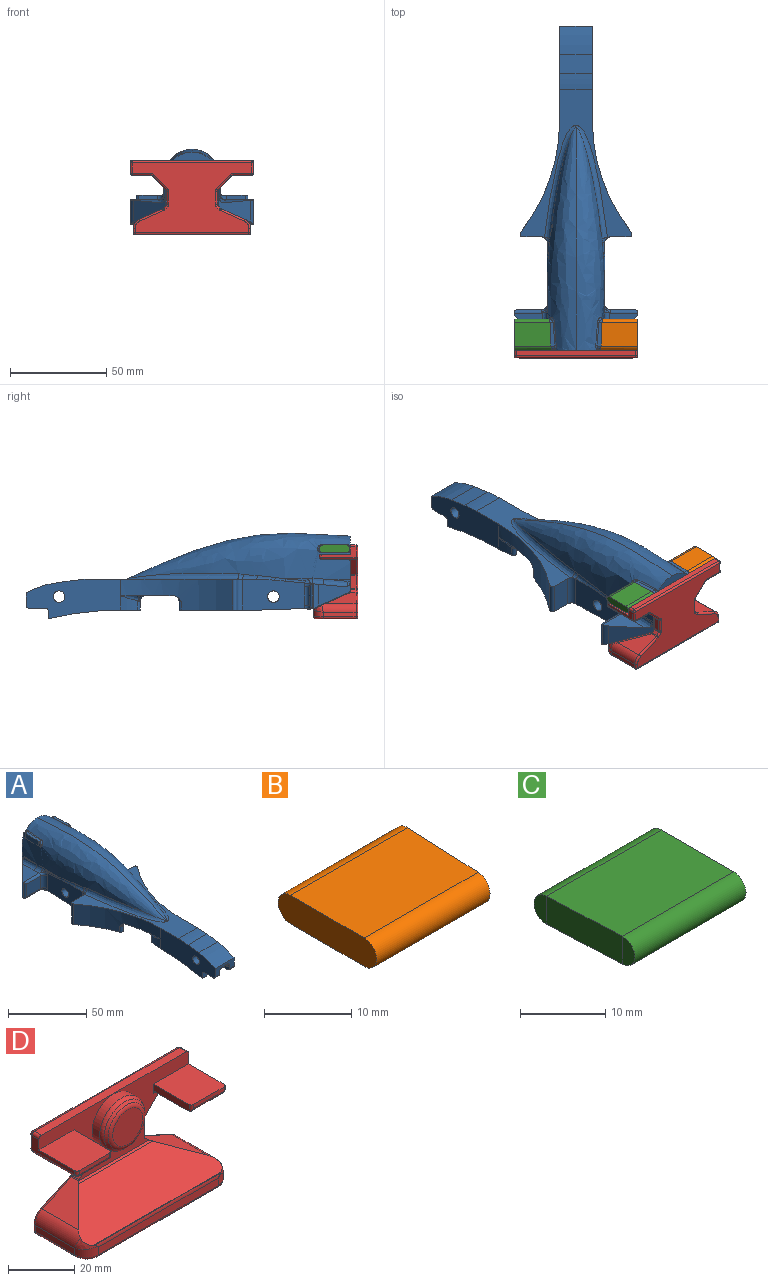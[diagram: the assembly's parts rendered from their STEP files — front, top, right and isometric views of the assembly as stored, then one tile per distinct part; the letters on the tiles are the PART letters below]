
ASSEMBLY  parts=4 mates=3
PART A: 206 faces, bbox 65.7x176.7x49.3 mm
  f0: extruded ~13.86x1.47mm, area 8mm2, adj f153,f156,f180,f181
  f1: extruded ~13.86x1.47mm, area 8mm2, adj f153,f154,f200,f201
  f2: plane 4.04x2.22mm, normal (-1,0.05,0), area 7.2mm2, adj f154,f158,f159,f167,f179
  f3: plane 3.74x2.02mm, normal (-1,0.04,0), area 6.6mm2, adj f4,f154,f158,f166,f174
  f4: plane 1.69x0.12mm, normal (0,-1,0), area 0.1mm2, adj f3,f154,f174
  f5: plane 12x2.55mm, normal (0,0,1), area 21.9mm2, adj f158,f166,f167,f176
  f6: plane 3.74x2.02mm, normal (1,0.04,0), area 6.6mm2, adj f156,f160,f161,f165,f168
  f7: plane 4.04x2.22mm, normal (1,0.05,0), area 7.2mm2, adj f8,f156,f160,f164,f173
  f8: plane 0.69x0.38mm, normal (0,1,0), area 0.1mm2, adj f7,f164,f173
  f9: plane 12x2.55mm, normal (0,0,1), area 21.9mm2, adj f160,f164,f165,f170
  f10: cylinder r=1.5mm len=7.39mm, axis (-1,0,0), area 10mm2, adj f93,f94,f141,f153
  f11: plane 77.19x58.27mm, normal (0,0,1), area 850.3mm2, adj f37,f38,f43,f45,f46,f47,f51,f52
  f12: cylinder r=1.5mm len=7.39mm, axis (-1,0,0), area 10mm2, adj f27,f84,f129,f153
  f13: plane 16.53x15.09mm, normal (0,0.09,1), area 127mm2, adj f94,f95,f96,f97,f144,f181,f182
  f14: cylinder r=3mm len=17mm, axis (-1,0,0), area 320.4mm2, adj f37,f38
  f15: plane 12.39x5.01mm, normal (0,-0.38,-0.93), area 40.5mm2, adj f16,f69,f99,f100,f101,f109,f110,f111
  f16: cylinder r=3mm len=9.64mm, axis (0,0.93,-0.38), area 38.5mm2, adj f15,f35,f39,f99,f150,f151
  f17: plane 32.43x16.02mm, normal (-1,0,0), area 455.3mm2, adj f31,f44,f64,f76,f82,f145,f146,f147
  f18: plane 17.44x4.22mm, normal (-1,0,0), area 15.6mm2, adj f92,f93,f98,f141
  f19: plane 17.44x4.22mm, normal (1,0,0), area 15.6mm2, adj f27,f28,f82,f129
  f20: plane 8.07x3.26mm, normal (-1,0,0), area 12.7mm2, adj f35,f61,f66,f109
  f21: plane 46.27x9mm, normal (1,0,0), area 142.9mm2, adj f41,f59,f67,f77,f78,f101,f102,f103
  f22: plane 38.6x16.7mm, normal (0,0.24,-0.97), area 601mm2, adj f71,f129,f130,f140,f141,f153
  f23: plane 28.21x4.5mm, normal (1,0,0), area 94.2mm2, adj f31,f50,f76,f123,f124,f125
  f24: cylinder r=30mm len=4.5mm, axis (0,0,-1), area 0.2mm2, adj f32,f54,f75,f133
  f25: plane 12.69x9.72mm, normal (0,-1,0), area 123.3mm2, adj f28,f30,f83,f146
  f26: plane 16.53x15.09mm, normal (0,0.09,1), area 127mm2, adj f30,f84,f85,f87,f147,f199,f200
  f27: plane 22.85x18.63mm, normal (0,0.41,-0.91), area 265.4mm2, adj f12,f19,f28,f84,f85,f129
  f28: cylinder r=1.5mm len=21.69mm, axis (-1,0,0), area 45.4mm2, adj f19,f25,f27,f29,f82,f83,f85,f86
  f29: plane 12.72x0.14mm, normal (-1,0,0), area 1.8mm2, adj f28,f30,f83,f86
  f30: cylinder r=1.5mm len=14.19mm, axis (1,0,0), area 34.1mm2, adj f25,f26,f29,f83,f86,f147
  f31: cylinder r=41.69mm len=4.5mm, axis (1,0,0), area 6.5mm2, adj f17,f23,f76,f82,f126
  f32: plane 28.21x4.5mm, normal (-1,0,0), area 94.2mm2, adj f24,f75,f81,f134,f135,f136
  f33: plane 51.59x25.23mm, normal (0,0,-1), area 736.5mm2, adj f45,f51,f73,f74,f105,f106,f116,f117
  f34: plane 46.27x9mm, normal (-1,0,0), area 142.9mm2, adj f40,f56,f65,f79,f80,f112,f113,f114
  f35: plane 17.01x6.48mm, normal (0,-1,0), area 69.2mm2, adj f16,f20,f37,f38,f39,f60,f61,f62
  f36: plane 32.44x16.02mm, normal (1,0,0), area 455.3mm2, adj f44,f63,f75,f81,f98,f142,f143,f144
  f37: plane 49.36x20.5mm, normal (-1,0,0), area 732.8mm2, adj f11,f14,f35,f41,f42,f43,f45,f58
  f38: plane 49.36x20.5mm, normal (1,0,0), area 732.8mm2, adj f11,f14,f35,f40,f42,f43,f51,f57
  f39: plane 8.07x3.26mm, normal (1,0,0), area 12.7mm2, adj f16,f35,f62,f68
  f40: plane 4x4mm, normal (0,-1,0), area 16mm2, adj f34,f38,f65,f79
  f41: plane 4x4mm, normal (0,-1,0), area 16mm2, adj f21,f37,f67,f78
  f42: plane 17x9.65mm, normal (0,-0.14,0.99), area 165.7mm2, adj f37,f38,f43,f60
  f43: cylinder r=60mm len=17mm, axis (1,0,0), area 144.7mm2, adj f11,f37,f38,f42
  f44: cylinder r=3mm len=30mm, axis (-1,0,0), area 565.5mm2, adj f17,f36
  f45: cylinder r=92.82mm len=57.94mm, axis (0,0,1), area 767.9mm2, adj f11,f33,f37,f47,f49,f76,f107,f108
  f46: plane 16x9.64mm, normal (0,1,0), area 154.2mm2, adj f11,f47,f64,f76
  f47: cylinder r=1.5mm len=16mm, axis (0,0,1), area 53.9mm2, adj f11,f45,f46,f76
  f48: cylinder r=136.18mm len=12.06mm, axis (0,0,-1), area 54.3mm2, adj f49,f50,f76,f121
  f49: cylinder r=1.5mm len=4.5mm, axis (0,0,1), area 18.3mm2, adj f45,f48,f76,f120
  f50: cylinder r=30mm len=4.5mm, axis (0,0,-1), area 0.2mm2, adj f23,f48,f76,f122
  f51: cylinder r=92.82mm len=57.94mm, axis (0,0,1), area 767.9mm2, adj f11,f33,f38,f53,f55,f75,f118,f119
  f52: plane 16x9.64mm, normal (0,1,0), area 154.2mm2, adj f11,f53,f63,f75
  f53: cylinder r=1.5mm len=16mm, axis (0,0,1), area 53.9mm2, adj f11,f51,f52,f75
  f54: cylinder r=136.18mm len=12.06mm, axis (0,0,-1), area 54.3mm2, adj f24,f55,f75,f132
  f55: cylinder r=1.5mm len=4.5mm, axis (0,0,1), area 18.3mm2, adj f51,f54,f75,f131
  f56: cylinder r=1.5mm len=4.84mm, axis (0,0,-1), area 19.8mm2, adj f34,f57,f80,f117,f118
  f57: cylinder r=37.75mm len=8.81mm, axis (0,0,-1), area 54.8mm2, adj f38,f56,f80,f119
  f58: cylinder r=37.75mm len=8.81mm, axis (0,0,-1), area 54.8mm2, adj f37,f59,f77,f108
  f59: cylinder r=1.5mm len=4.84mm, axis (0,0,-1), area 19.8mm2, adj f21,f58,f77,f106,f107
  f60: cylinder r=42.58mm len=17mm, axis (-1,0,0), area 268.4mm2, adj f35,f37,f38,f42
  f61: cylinder r=1.5mm len=4mm, axis (-1,0,0), area 9.4mm2, adj f20,f35,f38,f66
  f62: cylinder r=1.5mm len=4mm, axis (-1,0,0), area 9.4mm2, adj f35,f37,f39,f68
  f63: cylinder r=3mm len=16mm, axis (0,0,1), area 75.4mm2, adj f11,f36,f52,f75,f189
  f64: cylinder r=3mm len=16mm, axis (0,0,1), area 75.4mm2, adj f11,f17,f46,f76,f192
  f65: cylinder r=1.5mm len=4mm, axis (-1,0,0), area 9.4mm2, adj f34,f38,f40,f66,f111
  f66: plane 8.57x4.03mm, normal (0,0,-1), area 34.2mm2, adj f20,f38,f61,f65,f110
  f67: cylinder r=1.5mm len=4mm, axis (-1,0,0), area 9.4mm2, adj f21,f37,f41,f68,f100
  f68: plane 8.57x4.03mm, normal (0,0,-1), area 34.2mm2, adj f37,f39,f62,f67,f99
  f69: cylinder r=6mm len=3.81mm, axis (1,0,0), area 11.6mm2, adj f15,f70,f102,f113
  f70: plane 17.07x4.58mm, normal (0,0.26,-0.97), area 53mm2, adj f69,f74,f103,f114
  f71: cylinder r=6mm len=16.69mm, axis (1,0,0), area 55.6mm2, adj f22,f72,f128,f139
  f72: plane 16.03x10.19mm, normal (0,-0.32,-0.95), area 163.1mm2, adj f71,f73,f125,f126,f127,f136,f137,f138
  f73: cylinder r=50mm len=16.18mm, axis (-1,0,0), area 247.2mm2, adj f33,f72,f124,f135
  f74: cylinder r=50mm len=12.97mm, axis (1,0,0), area 39.3mm2, adj f33,f70,f104,f115
  f75: plane 40.66x18.64mm, normal (0,0,-1), area 358mm2, adj f24,f32,f36,f51,f52,f53,f54,f55
  f76: plane 40.66x18.64mm, normal (0,0,-1), area 358mm2, adj f17,f23,f31,f45,f46,f47,f48,f49
  f77: plane 9.96x4mm, normal (0,0,-1), area 34.7mm2, adj f21,f58,f59,f78
  f78: cylinder r=161.13mm len=37.81mm, axis (-1,0,0), area 152.7mm2, adj f21,f37,f41,f77
  f79: cylinder r=161.13mm len=37.81mm, axis (-1,0,0), area 152.7mm2, adj f34,f38,f40,f80
  f80: plane 9.96x4mm, normal (0,0,-1), area 34.7mm2, adj f34,f56,f57,f79
  f81: cylinder r=41.69mm len=4.5mm, axis (1,0,0), area 6.5mm2, adj f32,f36,f75,f98,f137
  f82: plane 28.76x8.77mm, normal (0,0.03,-1), area 127.9mm2, adj f17,f19,f28,f31,f127,f128,f130,f145
  f83: cylinder r=1.5mm len=12.72mm, axis (0,0,1), area 26.4mm2, adj f25,f28,f29,f30
  f84: plane 17.79x17.79mm, normal (-0.71,0.71,0), area 163.3mm2, adj f12,f26,f27,f85,f153,f200,f201
  f85: cylinder r=6mm len=12.61mm, axis (0,0,1), area 33.8mm2, adj f26,f27,f28,f84,f87
  f86: plane 12.7x0.01mm, normal (0,1,0), area 0.1mm2, adj f28,f29,f30,f87
  f87: cylinder r=1.5mm len=12.7mm, axis (0,0,1), area 4.2mm2, adj f26,f28,f85,f86
  f88: plane 12.7x0.01mm, normal (0,1,0), area 0.1mm2, adj f89,f92,f96,f97
  f89: plane 12.72x0.14mm, normal (1,0,0), area 1.8mm2, adj f88,f90,f92,f97
  f90: cylinder r=1.5mm len=12.72mm, axis (0,0,1), area 26.4mm2, adj f89,f91,f92,f97
  f91: plane 12.69x9.72mm, normal (0,-1,0), area 123.3mm2, adj f90,f92,f97,f143
  f92: cylinder r=1.5mm len=21.69mm, axis (1,0,0), area 45.4mm2, adj f18,f88,f89,f90,f91,f93,f95,f96
  f93: plane 22.85x18.63mm, normal (0,0.41,-0.91), area 265.4mm2, adj f10,f18,f92,f94,f95,f141
  f94: plane 17.78x17.78mm, normal (0.71,0.71,0), area 163.3mm2, adj f10,f13,f93,f95,f153,f180,f181
  f95: cylinder r=6mm len=12.61mm, axis (0,0,1), area 33.8mm2, adj f13,f92,f93,f94,f96
  f96: cylinder r=1.5mm len=12.7mm, axis (0,0,1), area 4.2mm2, adj f13,f88,f92,f95
  f97: cylinder r=1.5mm len=14.19mm, axis (-1,0,0), area 34.1mm2, adj f13,f88,f89,f90,f91,f144
  f98: plane 28.76x8.77mm, normal (0,0.03,-1), area 127.9mm2, adj f18,f36,f81,f92,f138,f139,f140,f142
  f99: bspline ~3.57x3.08mm, area 8.4mm2, adj f15,f16,f68,f100
  f100: bspline ~3.59x3.03mm, area 7.3mm2, adj f15,f67,f99,f101
  f101: cylinder r=3mm len=3.72mm, axis (0,0.93,-0.38), area 11.8mm2, adj f15,f21,f100,f102
  f102: torus R=9mm, axis (-1,0,0), area 21.6mm2, adj f21,f69,f101,f103
  f103: cylinder r=3mm len=17.85mm, axis (0,0.97,0.26), area 83.3mm2, adj f21,f70,f102,f104
  f104: torus R=47mm, axis (-1,0,0), area 60.5mm2, adj f21,f74,f103,f105
  f105: cylinder r=3mm len=8.98mm, axis (0,-1,0), area 42.3mm2, adj f21,f33,f104,f106
  f106: torus R=4.5mm, axis (0,0,1), area 28.9mm2, adj f33,f59,f105,f107
  f107: bspline ~3x2.79mm, area 3.8mm2, adj f45,f59,f106,f108
  f108: bspline ~10.19x2.76mm, area 10.1mm2, adj f45,f58,f107
  f109: cylinder r=3mm len=9.64mm, axis (0,0.93,-0.38), area 38.5mm2, adj f15,f20,f35,f110,f148,f149
  f110: bspline ~5.08x3.46mm, area 8.4mm2, adj f15,f66,f109,f111
  f111: bspline ~3.59x3.03mm, area 7.3mm2, adj f15,f65,f110,f112
  f112: cylinder r=3mm len=3.72mm, axis (0,0.93,-0.38), area 11.8mm2, adj f15,f34,f111,f113
  f113: torus R=9mm, axis (1,0,0), area 21.6mm2, adj f34,f69,f112,f114
  f114: cylinder r=3mm len=17.85mm, axis (0,0.97,0.26), area 83.3mm2, adj f34,f70,f113,f115
  f115: torus R=47mm, axis (1,0,0), area 60.5mm2, adj f34,f74,f114,f116
  f116: cylinder r=3mm len=8.98mm, axis (0,1,0), area 42.3mm2, adj f33,f34,f115,f117
  f117: torus R=4.5mm, axis (0,0,1), area 28.9mm2, adj f33,f56,f116,f118
  f118: bspline ~3x2.79mm, area 3.8mm2, adj f51,f56,f117,f119
  f119: bspline ~10.19x2.76mm, area 10.1mm2, adj f51,f57,f118
  f120: torus R=4.5mm, axis (0,0,1), area 24.2mm2, adj f33,f45,f49,f121
  f121: torus R=139.18mm, axis (0,0,1), area 57.4mm2, adj f33,f48,f120,f122
  f122: torus R=33mm, axis (0,0,1), area 0.2mm2, adj f33,f50,f121,f123
  f123: cylinder r=3mm len=7.28mm, axis (0,-1,0), area 34.3mm2, adj f23,f33,f122,f124
  f124: torus R=47mm, axis (-1,0,0), area 76mm2, adj f23,f73,f123,f125
  f125: cylinder r=3mm len=6.7mm, axis (0,0.95,-0.32), area 28.5mm2, adj f23,f72,f124,f126
  f126: bspline ~3x2.84mm, area 1.9mm2, adj f31,f72,f125,f127
  f127: bspline ~6.39x3.02mm, area 15.1mm2, adj f72,f82,f126,f128
  f128: bspline ~5.87x2.57mm, area 9.8mm2, adj f71,f82,f127,f130
  f129: cylinder r=3mm len=29.22mm, axis (0,-0.97,-0.24), area 121.9mm2, adj f12,f19,f22,f27,f130,f204
  f130: bspline ~10.78x3.27mm, area 36.9mm2, adj f22,f82,f128,f129
  f131: torus R=4.5mm, axis (0,0,1), area 24.2mm2, adj f33,f51,f55,f132
  f132: torus R=139.18mm, axis (0,0,1), area 57.4mm2, adj f33,f54,f131,f133
  f133: torus R=33mm, axis (0,0,1), area 0.2mm2, adj f24,f33,f132,f134
  f134: cylinder r=3mm len=7.28mm, axis (0,1,0), area 34.3mm2, adj f32,f33,f133,f135
  f135: torus R=47mm, axis (1,0,0), area 76mm2, adj f32,f73,f134,f136
  f136: cylinder r=3mm len=6.7mm, axis (0,0.95,-0.32), area 28.5mm2, adj f32,f72,f135,f137
  f137: bspline ~3.19x3.04mm, area 2mm2, adj f72,f81,f136,f138
  f138: bspline ~6.42x3.08mm, area 15.1mm2, adj f72,f98,f137,f139
  f139: bspline ~5.01x2.49mm, area 9.8mm2, adj f71,f98,f138,f140
  f140: bspline ~12.73x3.61mm, area 36.9mm2, adj f22,f98,f139,f141
  f141: cylinder r=3mm len=29.22mm, axis (0,-0.97,-0.24), area 121.9mm2, adj f10,f18,f22,f93,f140,f203
  f142: torus R=4.5mm, axis (-1,0,0), area 10.6mm2, adj f36,f92,f98,f143
  f143: cylinder r=3mm len=9.72mm, axis (0,0,1), area 45.8mm2, adj f36,f91,f142,f144
  f144: torus R=4.5mm, axis (-1,0,0), area 9.3mm2, adj f13,f36,f97,f143,f183,f184
  f145: torus R=4.5mm, axis (1,0,0), area 10.6mm2, adj f17,f28,f82,f146
  f146: cylinder r=3mm len=9.72mm, axis (0,0,1), area 45.8mm2, adj f17,f25,f145,f147
  f147: torus R=4.5mm, axis (1,0,0), area 9.3mm2, adj f17,f26,f30,f146,f197,f198
  f148: extruded ~4.21x2.6mm, area 9mm2, adj f15,f109,f149,f150,f152
  f149: extruded ~0.17x0.06mm, area 0mm2, adj f109,f148,f152
  f150: extruded ~4.21x2.6mm, area 9.1mm2, adj f15,f16,f148,f151,f152
  f151: extruded ~0.17x0.06mm, area 0mm2, adj f16,f150,f152
  f152: plane 8.57x1.99mm, normal (0,-1,0), area 7.2mm2, adj f35,f148,f149,f150,f151
  f153: plane 28.14x28.14mm, normal (0,1,0), area 416.3mm2, adj f0,f1,f10,f12,f22,f84,f94,f154
  f154: bspline ~127x31.96mm, area 2576.2mm2, adj f1,f2,f3,f4,f153,f155,f156,f158
  f155: extruded ~11.89x0.9mm, area 5.3mm2, adj f154,f196,f197
  f156: bspline ~127x31.96mm, area 2576.2mm2, adj f0,f6,f7,f153,f154,f157,f160,f161
  f157: extruded ~11.89x0.9mm, area 5.3mm2, adj f156,f184,f185
  f158: extruded ~12x3.96mm, area 46.2mm2, adj f2,f3,f5,f154
  f159: plane 0.69x0.38mm, normal (0,1,0), area 0.1mm2, adj f2,f167,f179
  f160: extruded ~12x3.96mm, area 46.2mm2, adj f6,f7,f9,f156
  f161: plane 1.69x0.12mm, normal (0,-1,0), area 0.1mm2, adj f6,f156,f168
  f162: cylinder r=9.5mm len=52mm, axis (0,1,0), area 3103.9mm2, adj f153,f163
  f163: plane 19x19mm, normal (0,1,0), area 283.5mm2, adj f162
  f164: cylinder r=2mm len=2.05mm, axis (1,0,0), area 4.3mm2, adj f7,f8,f9,f171,f172
  f165: cylinder r=2mm len=1.94mm, axis (1,0,0), area 2.2mm2, adj f6,f9,f169
  f166: cylinder r=2mm len=1.94mm, axis (-1,0,0), area 2.2mm2, adj f3,f5,f175
  f167: cylinder r=2mm len=2.05mm, axis (-1,0,0), area 4.3mm2, adj f2,f5,f159,f177,f178
  f168: bspline ~2.16x1.32mm, area 1.8mm2, adj f6,f156,f161,f169
  f169: bspline ~3.49x2.7mm, area 4.1mm2, adj f156,f165,f168,f170
  f170: bspline ~18.69x2.11mm, area 10.2mm2, adj f9,f156,f169,f171
  f171: bspline ~3.11x1.85mm, area 2mm2, adj f156,f164,f170,f172
  f172: bspline ~2.59x2.33mm, area 1.3mm2, adj f153,f164,f171,f173
  f173: bspline ~4.3x2.69mm, area 0.8mm2, adj f7,f8,f153,f172
  f174: bspline ~2.16x1.32mm, area 1.8mm2, adj f3,f4,f154,f175
  f175: bspline ~3.49x2.7mm, area 4.1mm2, adj f154,f166,f174,f176
  f176: bspline ~16.2x1.9mm, area 10.2mm2, adj f5,f154,f175,f177
  f177: bspline ~3.11x1.85mm, area 2mm2, adj f154,f167,f176,f178
  f178: bspline ~2.59x2.33mm, area 1.3mm2, adj f153,f167,f177,f179
  f179: bspline ~3.82x2.17mm, area 0.8mm2, adj f2,f153,f159,f178
  f180: bspline ~3.25x3.09mm, area 1.4mm2, adj f0,f94,f181
  f181: bspline ~31.24x5.91mm, area 58.4mm2, adj f0,f13,f94,f180,f182
  f182: bspline ~19.48x4.8mm, area 26.3mm2, adj f13,f156,f181,f183
  f183: bspline ~3.01x3mm, area 6.5mm2, adj f144,f156,f182,f184
  f184: bspline ~2.9x2.43mm, area 4.8mm2, adj f144,f157,f183,f185
  f185: bspline ~10.39x2.18mm, area 12.8mm2, adj f36,f157,f184,f186
  f186: bspline ~5.5x1.91mm, area 7.2mm2, adj f36,f156,f185,f187
  f187: bspline ~26.16x4.72mm, area 17mm2, adj f36,f156,f186,f188
  f188: bspline ~11.15x2.64mm, area 18.7mm2, adj f36,f156,f187,f189
  f189: bspline ~3.11x3.11mm, area 8.8mm2, adj f63,f156,f188,f190
  f190: bspline ~68.92x18.36mm, area 252.7mm2, adj f11,f156,f189,f191
  f191: bspline ~68.92x17.55mm, area 252.7mm2, adj f11,f154,f190,f192
  f192: bspline ~3.11x3.11mm, area 8.8mm2, adj f64,f154,f191,f193
  f193: bspline ~11.15x2.64mm, area 18.7mm2, adj f17,f154,f192,f194
  f194: bspline ~19.22x3.73mm, area 17mm2, adj f17,f154,f193,f195
  f195: bspline ~5.5x1.91mm, area 7.2mm2, adj f17,f154,f194,f196
  f196: bspline ~10.39x2.18mm, area 12.8mm2, adj f17,f155,f195,f197
  f197: bspline ~3.46x2.58mm, area 4.8mm2, adj f147,f155,f196,f198
  f198: bspline ~3.01x3mm, area 6.5mm2, adj f147,f154,f197,f199
  f199: bspline ~5.77x3.51mm, area 26.3mm2, adj f26,f154,f198,f200
  f200: bspline ~31.24x5.91mm, area 58.4mm2, adj f1,f26,f84,f199,f201
  f201: bspline ~3.25x3.09mm, area 1.4mm2, adj f1,f84,f200
  f202: plane 1.5x1.5mm, normal (-1,0,0), area 1.8mm2, adj f203
  f203: cylinder r=0.75mm len=5.34mm, axis (1,0,0), area 23mm2, adj f141,f202
  f204: cylinder r=0.75mm len=5.34mm, axis (1,0,0), area 23mm2, adj f129,f205
  f205: plane 1.5x1.5mm, normal (1,0,0), area 1.8mm2, adj f204
PART B: 8 faces, bbox 19.1x16x4 mm
  f0: cylinder r=2mm len=18.48mm, axis (-1,0,0), area 115.8mm2, adj f1,f3,f4,f5
  f1: plane 18.99x12mm, normal (0,0,1), area 224.7mm2, adj f0,f2,f4,f6
  f2: cylinder r=2mm len=19.09mm, axis (-1,0,0), area 119.7mm2, adj f1,f3,f4,f7
  f3: plane 18.99x12mm, normal (0,0,-1), area 224.7mm2, adj f0,f2,f4,f6
  f4: plane 16x4mm, normal (-1,0,0), area 60.6mm2, adj f0,f1,f2,f3
  f5: plane 4x2mm, normal (1,-0.04,0), area 6.3mm2, adj f0,f6
  f6: extruded ~12x4mm, area 48mm2, adj f1,f3,f5,f7
  f7: plane 4x2mm, normal (1,-0.05,0), area 6.3mm2, adj f2,f6
PART C: 8 faces, bbox 19.1x16x4 mm
  f0: plane 16x4mm, normal (1,0,0), area 60.6mm2, adj f1,f2,f3,f4
  f1: plane 18.99x12mm, normal (0,0,-1), area 224.7mm2, adj f0,f3,f4,f5
  f2: plane 18.99x12mm, normal (0,0,1), area 224.7mm2, adj f0,f3,f4,f5
  f3: cylinder r=2mm len=18.48mm, axis (1,0,0), area 115.8mm2, adj f0,f1,f2,f6
  f4: cylinder r=2mm len=19.09mm, axis (1,0,0), area 119.7mm2, adj f0,f1,f2,f7
  f5: extruded ~12x4mm, area 48mm2, adj f1,f2,f6,f7
  f6: plane 4x2mm, normal (-1,-0.04,0), area 6.3mm2, adj f3,f5
  f7: plane 4x2mm, normal (-1,-0.05,0), area 6.3mm2, adj f4,f5
PART D: 99 faces, bbox 64.3x23.8x39.3 mm
  f0: plane 12.99x1.5mm, normal (0,-1,0), area 19.5mm2, adj f20,f40,f42,f43
  f1: plane 7.47x7.47mm, normal (-0.71,0,-0.71), area 31.5mm2, adj f7,f56,f60,f66,f67
  f2: plane 15.18x3.5mm, normal (-1,0,0), area 38.2mm2, adj f7,f16,f23,f44,f61
  f3: plane 17.04x2.36mm, normal (-1,0,0), area 40.2mm2, adj f28,f30,f88,f89
  f4: plane 15.57x12.74mm, normal (-0.41,0,0.91), area 126.5mm2, adj f24,f25,f28,f79,f84
  f5: plane 15.57x12.74mm, normal (0.41,0,0.91), area 126.5mm2, adj f24,f25,f29,f82,f87
  f6: plane 17.04x2.36mm, normal (1,0,0), area 40.2mm2, adj f29,f31,f93,f98
  f7: plane 64x24.75mm, normal (0,-1,0), area 645.1mm2, adj f1,f2,f8,f11,f13,f14,f15,f17
  f8: cylinder r=9.25mm len=18.5mm, axis (0,1,0), area 184.3mm2, adj f7,f35
  f9: plane 12.84x12.84mm, normal (0,-1,0), area 129.5mm2, adj f36
  f10: plane 59.31x21.04mm, normal (0,0,-1), area 1241mm2, adj f89,f92,f94,f95,f97,f98
  f11: plane 6.59x3mm, normal (-1,0,0), area 19.8mm2, adj f7,f67,f72,f73
  f12: plane 18.18x13.99mm, normal (0,0,-1), area 236.6mm2, adj f21,f43,f52,f56,f59,f60
  f13: plane 18.18x5.5mm, normal (-1,0,0), area 39.3mm2, adj f7,f20,f41,f42,f51,f52
  f14: plane 62x3mm, normal (0,0,1), area 186mm2, adj f7,f41,f49,f50
  f15: plane 18.18x5.5mm, normal (1,0,0), area 39.3mm2, adj f7,f23,f48,f49,f57,f58
  f16: plane 18.18x13.99mm, normal (0,0,-1), area 236.6mm2, adj f2,f47,f57,f61,f64,f65
  f17: plane 6.59x3mm, normal (1,0,0), area 19.8mm2, adj f7,f70,f76,f77
  f18: plane 62x36.43mm, normal (0,1,0), area 1472.3mm2, adj f50,f51,f58,f59,f63,f65,f66,f68
  f19: plane 51.31x2.84mm, normal (0,-1,0), area 145.8mm2, adj f30,f31,f32,f95
  f20: plane 16.18x14.99mm, normal (0,0,1), area 242.1mm2, adj f0,f7,f13,f21,f40,f42
  f21: plane 15.18x3.5mm, normal (1,0,0), area 38.2mm2, adj f7,f12,f20,f40,f56
  f22: plane 12.99x1.5mm, normal (0,-1,0), area 19.5mm2, adj f23,f44,f47,f48
  f23: plane 16.18x14.99mm, normal (0,0,1), area 242.1mm2, adj f2,f7,f15,f22,f44,f48
  f24: plane 59.12x18.31mm, normal (0,-0.41,0.91), area 954.8mm2, adj f4,f5,f25,f26,f28,f29,f33,f34
  f25: cylinder r=2mm len=31.83mm, axis (1,0,0), area 26.4mm2, adj f4,f5,f7,f24,f79,f82
  f26: extruded ~54.47x0.2mm, area 11.3mm2, adj f24,f32,f33,f34
  f27: cone r=7.25mm half-angle=45deg, axis (0,1,0), area 60.7mm2, adj f35,f36
  f28: cylinder r=5mm len=17.75mm, axis (0,1,0), area 98.7mm2, adj f3,f4,f24,f33,f86
  f29: cylinder r=5mm len=17.75mm, axis (0,1,0), area 98.7mm2, adj f5,f6,f24,f34,f90
  f30: cylinder r=5mm len=5mm, axis (0,0,-1), area 22.6mm2, adj f3,f19,f32,f33,f92
  f31: cylinder r=5mm len=5mm, axis (0,0,1), area 22.6mm2, adj f6,f19,f32,f34,f97
  f32: cylinder r=5mm len=53.15mm, axis (1,0,0), area 65.3mm2, adj f19,f26,f30,f31,f33,f34
  f33: bspline ~4.99x4.99mm, area 12.9mm2, adj f24,f26,f28,f30,f32
  f34: bspline ~4.99x4.99mm, area 12.9mm2, adj f24,f26,f29,f31,f32
  f35: torus R=7.25mm, axis (0,-1,0), area 89.3mm2, adj f8,f27
  f36: torus R=6.42mm, axis (0,-1,0), area 70.7mm2, adj f9,f27
  f37: plane 3x1.46mm, normal (-0.71,0,0.71), area 6.2mm2, adj f7,f73,f78,f79
  f38: plane 3x1.46mm, normal (0.71,0,0.71), area 6.2mm2, adj f7,f76,f82,f83
  f39: plane 7.47x7.47mm, normal (0.71,0,-0.71), area 31.5mm2, adj f7,f61,f64,f70,f71
  f40: cylinder r=1mm len=2.5mm, axis (0,0,-1), area 3.1mm2, adj f0,f20,f21,f43
  f41: cylinder r=1mm len=3mm, axis (0,-1,0), area 4.7mm2, adj f7,f13,f14,f45
  f42: cylinder r=1mm len=1.5mm, axis (0,0,-1), area 2.4mm2, adj f0,f13,f20,f46
  f43: cylinder r=1mm len=13.99mm, axis (1,0,0), area 21.2mm2, adj f0,f12,f40,f46
  f44: cylinder r=1mm len=2.5mm, axis (0,0,1), area 3.1mm2, adj f2,f22,f23,f47
  f45: sphere r=1mm, area 1.6mm2, adj f41,f50,f51
  f46: sphere r=1mm, area 1.6mm2, adj f42,f43,f52
  f47: cylinder r=1mm len=13.99mm, axis (-1,0,0), area 21.2mm2, adj f16,f22,f44,f53
  f48: cylinder r=1mm len=1.5mm, axis (0,0,1), area 2.4mm2, adj f15,f22,f23,f53
  f49: cylinder r=1mm len=3mm, axis (0,1,0), area 4.7mm2, adj f7,f14,f15,f54
  f50: cylinder r=1mm len=62mm, axis (-1,0,0), area 97.4mm2, adj f14,f18,f45,f54
  f51: cylinder r=1mm len=5.5mm, axis (0,0,-1), area 8.6mm2, adj f13,f18,f45,f55
  f52: cylinder r=1mm len=18.18mm, axis (0,1,0), area 28.6mm2, adj f12,f13,f46,f55
  f53: sphere r=1mm, area 1.6mm2, adj f47,f48,f57
  f54: sphere r=1mm, area 1mm2, adj f49,f50,f58
  f55: sphere r=1mm, area 2.1mm2, adj f51,f52,f59
  f56: cylinder r=1mm len=4.41mm, axis (-1,0,0), area 5.8mm2, adj f1,f7,f12,f21,f60
  f57: cylinder r=1mm len=18.18mm, axis (0,1,0), area 28.6mm2, adj f15,f16,f53,f62
  f58: cylinder r=1mm len=5.5mm, axis (0,0,1), area 8.6mm2, adj f15,f18,f54,f62
  f59: cylinder r=1mm len=9.58mm, axis (1,0,0), area 15mm2, adj f12,f18,f55,f63
  f60: cylinder r=1mm len=4mm, axis (0,1,0), area 2.9mm2, adj f1,f12,f56,f63
  f61: cylinder r=1mm len=4.41mm, axis (-1,0,0), area 5.8mm2, adj f2,f7,f16,f39,f64
  f62: sphere r=1mm, area 1.6mm2, adj f57,f58,f65
  f63: torus R=2mm, axis (0,1,0), area 1.7mm2, adj f18,f59,f60,f66
  f64: cylinder r=1mm len=4mm, axis (0,1,0), area 2.9mm2, adj f16,f39,f61,f68
  f65: cylinder r=1mm len=9.58mm, axis (1,0,0), area 15mm2, adj f16,f18,f62,f68
  f66: cylinder r=1mm len=8.12mm, axis (0.71,0,-0.71), area 16.5mm2, adj f1,f18,f63,f69
  f67: cylinder r=1mm len=3mm, axis (0,1,0), area 2.4mm2, adj f1,f7,f11,f69
  f68: torus R=2mm, axis (0,1,0), area 1.7mm2, adj f18,f64,f65,f71
  f69: torus R=2mm, axis (0,1,0), area 1.7mm2, adj f18,f66,f67,f72
  f70: cylinder r=1mm len=3mm, axis (0,1,0), area 2.4mm2, adj f7,f17,f39,f74
  f71: cylinder r=1mm len=8.12mm, axis (0.71,0,0.71), area 16.5mm2, adj f18,f39,f68,f74
  f72: cylinder r=1mm len=6.59mm, axis (0,0,-1), area 10.3mm2, adj f11,f18,f69,f75
  f73: cylinder r=1mm len=3mm, axis (0,1,0), area 2.4mm2, adj f7,f11,f37,f75
  f74: torus R=2mm, axis (0,1,0), area 1.7mm2, adj f18,f70,f71,f77
  f75: torus R=2mm, axis (0,1,0), area 1.7mm2, adj f18,f72,f73,f78
  f76: cylinder r=1mm len=3mm, axis (0,1,0), area 2.4mm2, adj f7,f17,f38,f80
  f77: cylinder r=1mm len=6.59mm, axis (0,0,1), area 10.3mm2, adj f17,f18,f74,f80
  f78: cylinder r=1mm len=2.16mm, axis (0.71,0,0.71), area 3.2mm2, adj f18,f37,f75,f81
  f79: cylinder r=1mm len=3.12mm, axis (0,1,0), area 1.1mm2, adj f4,f7,f25,f37,f81
  f80: torus R=2mm, axis (0,1,0), area 1.7mm2, adj f18,f76,f77,f83
  f81: torus R=2mm, axis (0,1,0), area 0.8mm2, adj f18,f78,f79,f84
  f82: cylinder r=1mm len=3.12mm, axis (0,-1,0), area 1.1mm2, adj f5,f7,f25,f38,f85
  f83: cylinder r=1mm len=2.16mm, axis (0.71,0,-0.71), area 3.2mm2, adj f18,f38,f80,f85
  f84: cylinder r=1mm len=13.04mm, axis (-0.91,0,-0.41), area 21.7mm2, adj f4,f18,f81,f86
  f85: torus R=2mm, axis (0,1,0), area 0.8mm2, adj f18,f82,f83,f87
  f86: torus R=4mm, axis (0,1,0), area 8.4mm2, adj f18,f28,f84,f88
  f87: cylinder r=1mm len=13.04mm, axis (-0.91,0,0.41), area 21.7mm2, adj f5,f18,f85,f90
  f88: cylinder r=1mm len=2.36mm, axis (0,0,-1), area 3.7mm2, adj f3,f18,f86,f91
  f89: cylinder r=1mm len=17.04mm, axis (0,1,0), area 26.8mm2, adj f3,f10,f91,f92
  f90: torus R=4mm, axis (0,1,0), area 8.4mm2, adj f18,f29,f87,f93
  f91: sphere r=1mm, area 2.1mm2, adj f88,f89,f94
  f92: torus R=4mm, axis (0,0,-1), area 11.4mm2, adj f10,f30,f89,f95
  f93: cylinder r=1mm len=2.36mm, axis (0,0,1), area 3.7mm2, adj f6,f18,f90,f96
  f94: cylinder r=1mm len=59.31mm, axis (1,0,0), area 93.2mm2, adj f10,f18,f91,f96
  f95: cylinder r=1mm len=51.31mm, axis (-1,0,0), area 80.6mm2, adj f10,f19,f92,f97
  f96: sphere r=1mm, area 1mm2, adj f93,f94,f98
  f97: torus R=4mm, axis (0,0,-1), area 11.4mm2, adj f10,f31,f95,f98
  f98: cylinder r=1mm len=17.04mm, axis (0,-1,0), area 26.8mm2, adj f6,f10,f96,f97
PLACE A rot(axis=(0,0,1),180deg) t=(0,0,0)mm
PLACE B rot(axis=(0,0,1),180deg) t=(0,0,0)mm
PLACE C rot(axis=(0,0,1),180deg) t=(0,0,0)mm
PLACE D rot(axis=(0,0,1),180deg) t=(0,0,0)mm
MATE fastened B.f1 <-> A.f5  axis (0,0,1) through (13.31,8.76,9.43)mm
MATE fastened D.f8 <-> A.f162  axis (0,1,0) through (0,0,0)mm
MATE fastened C.f2 <-> A.f9  axis (0,0,1) through (-13.31,8.76,9.43)mm
